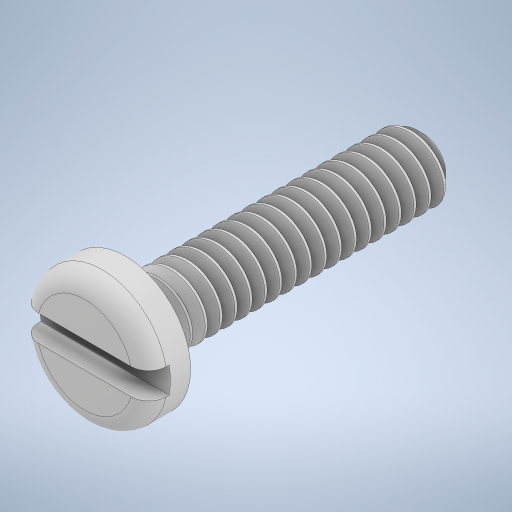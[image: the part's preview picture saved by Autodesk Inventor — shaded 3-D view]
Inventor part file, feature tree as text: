
AUTODESK INVENTOR PART (.ipt)
format: ipt  version: 2024 (Build 280153000, 153)  size: 731,648 bytes
history: native  units: in
note: dims shown in document units (in); Inventor stores cm internally (conversion verified against a paired STEP export)
features: other x1, extrude x1
ambient origin geometry x8: Origin, YZ Plane, XZ Plane, XY Plane, X Axis, Y Axis, Z Axis, Center Point
bodies: Solid1 (feature_tree)
feature tree (2):
  other  "Plane1"
  extrude  "Extrude15"  [1 undecoded]
note: 1 required parameter value undecoded (feature->parameter linkage not recoverable at this tier; creation-order binding heuristic only, values carry confidence <= 0.55)
